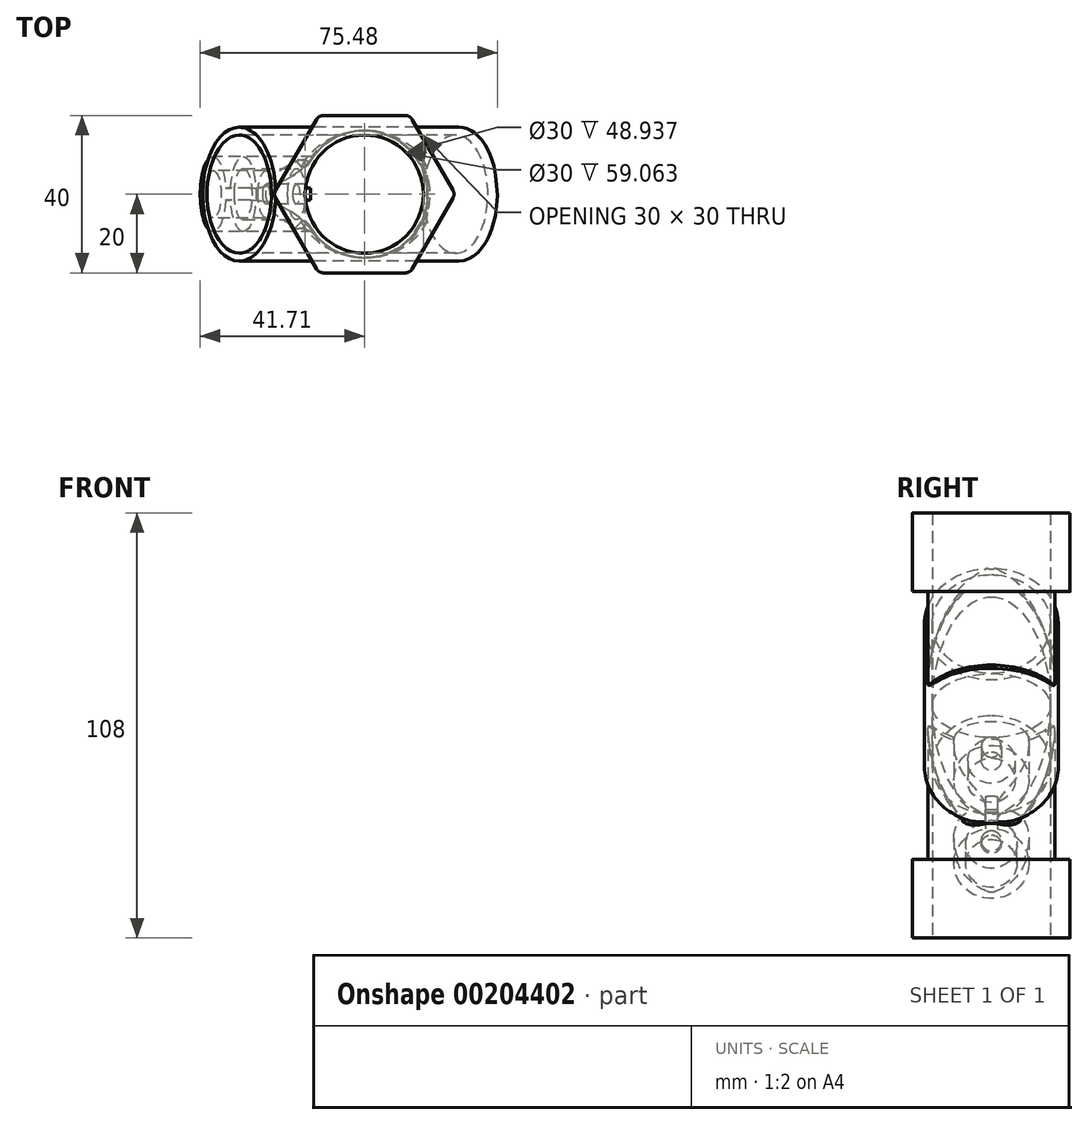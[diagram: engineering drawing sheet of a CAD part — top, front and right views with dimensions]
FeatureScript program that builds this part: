
annotation { "Feature Type Name" : "Feature", "Feature Type Description" : "" }
export const myFeature = defineFeature(function(context is Context, id is Id, definition is map)
    precondition{}
    {
        {
            var Q0;
            Q0=qCreatedBy(makeId("Top.planeOp"),FACE);
            var sketch = newSketch(context, id + "F0", { "sketchPlane" : qUnion([Q0])});
            skCircle(sketch, "E0", {"center": v(0, 0) * mm, "radius": 15 * mm});
            skCircle(sketch, "E1.cCircle", {"center": v(0, 0) * mm, "radius": 20 * mm, "construction": true});
            skLineSegment(sketch, "E1.0", {"start": v(10.4, -20) * mm, "end": v(-10.4, -20) * mm});
            skLineSegment(sketch, "E1.1", {"start": v(-12.12, -19) * mm, "end": v(-22.52, -1) * mm});
            skLineSegment(sketch, "E1.2", {"start": v(-22.52, 1) * mm, "end": v(-12.12, 19) * mm});
            skLineSegment(sketch, "E1.3", {"start": v(-10.4, 20) * mm, "end": v(10.4, 20) * mm});
            skLineSegment(sketch, "E1.4", {"start": v(12.12, 19) * mm, "end": v(22.52, 1) * mm});
            skLineSegment(sketch, "E1.5", {"start": v(22.52, -1) * mm, "end": v(12.12, -19) * mm});
            skPoint(sketch, "E1.0.midPoint", {"position": v(0, -20) * mm});
            skPoint(sketch, "E2.visualSharp", {"position": v(-23.1, 0) * mm});
            skArc(sketch, "E2.filletArc", {"start": v(-22.52, 1) * mm, "mid": v(-22.78, 0) * mm, "end": v(-22.52, -1) * mm});
            skPoint(sketch, "E3.visualSharp", {"position": v(-11.55, -20) * mm});
            skArc(sketch, "E3.filletArc", {"start": v(-12.12, -19) * mm, "mid": v(-11.4, -19.73) * mm, "end": v(-10.4, -20) * mm});
            skPoint(sketch, "E4.visualSharp", {"position": v(11.55, -20) * mm});
            skArc(sketch, "E4.filletArc", {"start": v(10.4, -20) * mm, "mid": v(11.4, -19.73) * mm, "end": v(12.12, -19) * mm});
            skPoint(sketch, "E5.visualSharp", {"position": v(23.1, 0) * mm});
            skArc(sketch, "E5.filletArc", {"start": v(22.52, -1) * mm, "mid": v(22.78, 0) * mm, "end": v(22.52, 1) * mm});
            skPoint(sketch, "E6.visualSharp", {"position": v(11.55, 20) * mm});
            skArc(sketch, "E6.filletArc", {"start": v(12.12, 19) * mm, "mid": v(11.4, 19.73) * mm, "end": v(10.4, 20) * mm});
            skPoint(sketch, "E7.visualSharp", {"position": v(-11.55, 20) * mm});
            skArc(sketch, "E7.filletArc", {"start": v(-10.4, 20) * mm, "mid": v(-11.4, 19.73) * mm, "end": v(-12.12, 19) * mm});
            skSolve(sketch);
        }
        {
            var Q0;
            Q0=makeQuery(id+"F0.imprint","IMPRINT",FACE,{"disambiguationData":[TD([[makeQuery(id+"F0.imprint","IMPRINT",EDGE,{"derivedFrom":sQuery(id+"F0.wireOp",EDGE,"E0")}),-1.0]])]});
            extrude(context, id + "F1", {"entities" : qUnion([Q0]), "depth" : 20 * mm});
        }
        {
            var Q0;
            Q0=makeQuery(id+"F1.opExtrude","CAP_FACE",FACE,{"disambiguationData":[OSD([sQuery(id+"F0.wireOp",EDGE,"E0"),sQuery(id+"F0.wireOp",EDGE,"E1.0"),sQuery(id+"F0.wireOp",EDGE,"E1.1"),sQuery(id+"F0.wireOp",EDGE,"E1.2"),sQuery(id+"F0.wireOp",EDGE,"E1.3"),sQuery(id+"F0.wireOp",EDGE,"E1.4"),sQuery(id+"F0.wireOp",EDGE,"E1.5"),sQuery(id+"F0.wireOp",EDGE,"E2.filletArc"),sQuery(id+"F0.wireOp",EDGE,"E3.filletArc"),sQuery(id+"F0.wireOp",EDGE,"E4.filletArc"),sQuery(id+"F0.wireOp",EDGE,"E5.filletArc"),sQuery(id+"F0.wireOp",EDGE,"E6.filletArc"),sQuery(id+"F0.wireOp",EDGE,"E7.filletArc")])],"isStart":false});
            var sketch = newSketch(context, id + "F2", { "sketchPlane" : qUnion([Q0])});
            skCircle(sketch, "E8", {"center": v(0, 0) * mm, "radius": 16.15 * mm});
            skCircle(sketch, "E9", {"center": v(0, 0) * mm, "radius": 9 * mm});
            skSolve(sketch);
        }
        {
            var Q0;
            Q0=makeQuery(id+"F2.imprint","IMPRINT",FACE,{"disambiguationData":[TD([[makeQuery(id+"F2.imprint","IMPRINT",EDGE,{"derivedFrom":sQuery(id+"F2.wireOp",EDGE,"E8")}),1.0]])]});
            var Q1;
            Q1=makeQuery(id+"F2.imprint","IMPRINT",FACE,{"disambiguationData":[TD([[makeQuery(id+"F2.imprint","IMPRINT",EDGE,{"derivedFrom":sQuery(id+"F2.wireOp",EDGE,"E9")}),-1.0]])]});
            extrude(context, id + "F3", {"entities" : qUnion([Q0, Q1]), "operationType" : NewBodyOperationType.ADD, "depth" : 34 * mm});
        }
        {
            var Q0;
            Q0=makeQuery(id+"F1.opExtrude","SWEPT_BODY",BODY,{"disambiguationData":[OSD([sQuery(id+"F0.wireOp",EDGE,"E0"),sQuery(id+"F0.wireOp",EDGE,"E1.0"),sQuery(id+"F0.wireOp",EDGE,"E1.1"),sQuery(id+"F0.wireOp",EDGE,"E1.2"),sQuery(id+"F0.wireOp",EDGE,"E1.3"),sQuery(id+"F0.wireOp",EDGE,"E1.4"),sQuery(id+"F0.wireOp",EDGE,"E1.5"),sQuery(id+"F0.wireOp",EDGE,"E2.filletArc"),sQuery(id+"F0.wireOp",EDGE,"E3.filletArc"),sQuery(id+"F0.wireOp",EDGE,"E4.filletArc"),sQuery(id+"F0.wireOp",EDGE,"E5.filletArc"),sQuery(id+"F0.wireOp",EDGE,"E6.filletArc"),sQuery(id+"F0.wireOp",EDGE,"E7.filletArc")])]});
            var Q1;
            Q1=makeQuery(id+"F3.opExtrude","CAP_FACE",FACE,{"disambiguationData":[OSD([sQuery(id+"F2.wireOp",EDGE,"E8"),sQuery(id+"F2.wireOp",EDGE,"E9")])],"isStart":false});
            mirror(context, id + "F4", {"operationType" : NewBodyOperationType.ADD, "entities" : qUnion([Q0]), "mirrorPlane" : qUnion([Q1])});
        }
        {
            var Q0;
            Q0=qCreatedBy(makeId("Front.planeOp"),FACE);
            var sketch = newSketch(context, id + "F5", { "sketchPlane" : qUnion([Q0])});
            skLineSegment(sketch, "E10", {"start": v(-22.52, 94) * mm, "end": v(33.32, 57.66) * mm});
            skLineSegment(sketch, "E11", {"start": v(16.15, 88) * mm, "end": v(16.15, 34) * mm, "construction": true});
            skLineSegment(sketch, "E12", {"start": v(-29.56, 78.3) * mm, "end": v(24.88, 42.87) * mm, "construction": true});
            skLineSegment(sketch, "E13", {"start": v(33.6, 56.28) * mm, "end": v(24.88, 42.87) * mm});
            skLineSegment(sketch, "E14", {"start": v(24.88, 42.87) * mm, "end": v(16.15, 29.46) * mm, "construction": true});
            skLineSegment(sketch, "E15", {"start": v(16.15, 29.46) * mm, "end": v(-42.19, 67.43) * mm, "construction": true});
            skLineSegment(sketch, "E16.0", {"start": v(31.39, 56.53) * mm, "end": v(23.2, 43.96) * mm});
            skLineSegment(sketch, "E16.1", {"start": v(-23.6, 92.32) * mm, "end": v(31.39, 56.53) * mm});
            skLineSegment(sketch, "E17", {"start": v(-22.52, 94) * mm, "end": v(-23.6, 92.32) * mm});
            skLineSegment(sketch, "E18", {"start": v(23.2, 43.96) * mm, "end": v(24.88, 42.87) * mm});
            skPoint(sketch, "E19.visualSharp", {"position": v(34.15, 57.12) * mm});
            skLineSegment(sketch, "E20", {"start": v(-23.6, 92.32) * mm, "end": v(-31.79, 79.75) * mm});
            skLineSegment(sketch, "E21", {"start": v(-31.79, 79.75) * mm, "end": v(23.2, 43.96) * mm});
            skArc(sketch, "E22.filletArc", {"start": v(33.6, 56.28) * mm, "mid": v(33.75, 57.03) * mm, "end": v(33.32, 57.66) * mm});
            skSolve(sketch);
        }
        {
            var Q0;
            Q0=makeQuery(id+"F5.imprint","IMPRINT",FACE,{"disambiguationData":[TD([[makeQuery(id+"F5.imprint","IMPRINT",EDGE,{"derivedFrom":sQuery(id+"F5.wireOp",EDGE,"E10")}),-1.0]])]});
            var Q1;
            Q1=sQuery(id+"F5.wireOp",EDGE,"E12");
            revolve(context, id + "F6", {"entities" : qUnion([Q0]), "axis" : qUnion([Q1]), "revolveType" : RevolveType.FULL});
        }
        {
            var Q0;
            Q0=makeQuery(id+"F5.imprint","IMPRINT",FACE,{"disambiguationData":[TD([[makeQuery(id+"F5.imprint","IMPRINT",EDGE,{"derivedFrom":sQuery(id+"F5.wireOp",EDGE,"E16.0")}),-1.0]])]});
            var Q1;
            Q1=sQuery(id+"F5.wireOp",EDGE,"E21");
            revolve(context, id + "F7", {"operationType" : NewBodyOperationType.REMOVE, "entities" : qUnion([Q0]), "axis" : qUnion([Q1]), "revolveType" : RevolveType.FULL, "oppositeDirection" : true});
        }
        {
            var Q0;
            Q0=makeQuery(id+"F4.opPattern","COPY",FACE,{"derivedFrom":makeQuery(id+"F3.opExtrude","CAP_FACE",FACE,{"disambiguationData":[OSD([sQuery(id+"F2.wireOp",EDGE,"E8"),sQuery(id+"F2.wireOp",EDGE,"E9")])],"isStart":true}),"instanceName":"1"});
            var sketch = newSketch(context, id + "F8", { "sketchPlane" : qUnion([Q0])});
            skCircle(sketch, "E23", {"center": v(0, 0) * mm, "radius": 15 * mm});
            skSolve(sketch);
        }
        {
            var Q0;
            Q0 = qSketchRegion(id + "F8", true);
            extrude(context, id + "F9", {"entities" : qUnion([Q0]), "operationType" : NewBodyOperationType.REMOVE, "depth" : 25 * mm});
        }
        {
            var Q0;
            Q0 = qSketchRegion(id + "F8", true);
            var Q1;
            Q1=makeQuery(id+"F4.opPattern","COPY",FACE,{"derivedFrom":makeQuery(id+"F3.opExtrude","CAP_FACE",FACE,{"disambiguationData":[OSD([sQuery(id+"F2.wireOp",EDGE,"E8"),sQuery(id+"F2.wireOp",EDGE,"E9")])],"isStart":true}),"instanceName":"1"});
            extrude(context, id + "F10", {"entities" : qUnion([Q0, Q1]), "operationType" : NewBodyOperationType.REMOVE, "oppositeDirection" : true, "depth" : 7 * mm});
        }
        {
            var Q0;
            Q0=makeQuery(id+"F6.opRevolve","SWEPT_BODY",BODY,{"disambiguationData":[OSD([sQuery(id+"F5.wireOp",EDGE,"E10"),sQuery(id+"F5.wireOp",EDGE,"E13"),sQuery(id+"F5.wireOp",EDGE,"E16.0"),sQuery(id+"F5.wireOp",EDGE,"E16.1"),sQuery(id+"F5.wireOp",EDGE,"E17"),sQuery(id+"F5.wireOp",EDGE,"E18"),sQuery(id+"F5.wireOp",EDGE,"E19.filletArc")])]});
            var Q1;
            Q1=makeQuery(id+"F1.opExtrude","SWEPT_BODY",BODY,{"disambiguationData":[OSD([sQuery(id+"F0.wireOp",EDGE,"E0"),sQuery(id+"F0.wireOp",EDGE,"E1.0"),sQuery(id+"F0.wireOp",EDGE,"E1.1"),sQuery(id+"F0.wireOp",EDGE,"E1.2"),sQuery(id+"F0.wireOp",EDGE,"E1.3"),sQuery(id+"F0.wireOp",EDGE,"E1.4"),sQuery(id+"F0.wireOp",EDGE,"E1.5"),sQuery(id+"F0.wireOp",EDGE,"E2.filletArc"),sQuery(id+"F0.wireOp",EDGE,"E3.filletArc"),sQuery(id+"F0.wireOp",EDGE,"E4.filletArc"),sQuery(id+"F0.wireOp",EDGE,"E5.filletArc"),sQuery(id+"F0.wireOp",EDGE,"E6.filletArc"),sQuery(id+"F0.wireOp",EDGE,"E7.filletArc")])]});
            booleanBodies(context, id + "F11", {"operationType" : BooleanOperationType.UNION, "tools" : qUnion([Q0, Q1])});
        }
        {
            var Q0;
            Q0=makeQuery(id+"F4.opPattern","COPY",EDGE,{"derivedFrom":makeQuery(id+"F3.opExtrude","CAP_EDGE",EDGE,{"disambiguationData":[OSD([sQuery(id+"F2.wireOp",EDGE,"E8")])],"isStart":true}),"instanceName":"1"});
            var Q1;
            Q1=makeQuery(id+"F3.opExtrude","CAP_EDGE",EDGE,{"disambiguationData":[OSD([sQuery(id+"F2.wireOp",EDGE,"E8")])],"isStart":true});
            var Q2;
            Q2=makeQuery(id+"F4.opPattern","COPY",EDGE,{"derivedFrom":makeQuery(id+"F3.opExtrude","CAP_EDGE",EDGE,{"disambiguationData":[OSD([sQuery(id+"F2.wireOp",EDGE,"E9")])],"isStart":true}),"instanceName":"1"});
            var Q3;
            Q3=makeQuery(id+"F3.opExtrude","CAP_EDGE",EDGE,{"disambiguationData":[OSD([sQuery(id+"F2.wireOp",EDGE,"E9")])],"isStart":true});
            chamfer(context, id + "F12", {"entities" : qUnion([Q0, Q1, Q2, Q3]), "width" : 7 * mm, "tangentPropagation" : true});
        }
        {
            var Q0;
            Q0=qCreatedBy(makeId("Top.planeOp"),FACE);
            var sketch = newSketch(context, id + "F13", { "sketchPlane" : qUnion([Q0])});
            skCircle(sketch, "E24", {"center": v(0, 0) * mm, "radius": 9 * mm});
            skSolve(sketch);
        }
        {
            var Q0;
            Q0 = qSketchRegion(id + "F13", true);
            extrude(context, id + "F14", {"entities" : qUnion([Q0]), "operationType" : NewBodyOperationType.REMOVE, "depth" : 100 * mm});
        }
        {
            var Q0;
            Q0=qCreatedBy(makeId("Front.planeOp"),FACE);
            var sketch = newSketch(context, id + "F15", { "sketchPlane" : qUnion([Q0])});
            skLineSegment(sketch, "E25", {"start": v(0, 90.32) * mm, "end": v(0, -35.6) * mm, "construction": true});
            skLineSegment(sketch, "E26", {"start": v(-32.67, 10) * mm, "end": v(0, 10) * mm, "construction": true});
            skLineSegment(sketch, "E27", {"start": v(-27.52, 10) * mm, "end": v(-39.63, 43.27) * mm, "construction": true});
            skLineSegment(sketch, "E28", {"start": v(-27.52, 10) * mm, "end": v(-0.04, 20) * mm});
            skLineSegment(sketch, "E29", {"start": v(-0.04, 20) * mm, "end": v(-1.2, 23.22) * mm});
            skLineSegment(sketch, "E30", {"start": v(-28.54, 12.82) * mm, "end": v(-27.52, 10) * mm});
            skLineSegment(sketch, "E31", {"start": v(-30.77, 18.93) * mm, "end": v(-9.94, 26.5) * mm, "construction": true});
            skLineSegment(sketch, "E32", {"start": v(-35.21, 31.14) * mm, "end": v(-3.62, 42.64) * mm});
            skLineSegment(sketch, "E33", {"start": v(-38.46, 40.07) * mm, "end": v(-7.1, 51.48) * mm, "construction": true});
            skLineSegment(sketch, "E34", {"start": v(-1.2, 23.22) * mm, "end": v(-2.43, 26.58) * mm});
            skLineSegment(sketch, "E35", {"start": v(-2.43, 26.58) * mm, "end": v(-16.4, 21.5) * mm});
            skLineSegment(sketch, "E36", {"start": v(-16.4, 21.5) * mm, "end": v(-15.02, 17.74) * mm});
            skLineSegment(sketch, "E37", {"start": v(-15.02, 17.74) * mm, "end": v(-28.54, 12.82) * mm});
            skLineSegment(sketch, "E38", {"start": v(-35.21, 31.14) * mm, "end": v(-36.4, 34.42) * mm});
            skLineSegment(sketch, "E39", {"start": v(-36.4, 34.42) * mm, "end": v(-22.88, 39.34) * mm});
            skLineSegment(sketch, "E40", {"start": v(-22.88, 39.34) * mm, "end": v(-24.09, 42.64) * mm});
            skLineSegment(sketch, "E41", {"start": v(-24.09, 42.64) * mm, "end": v(-15.16, 45.89) * mm});
            skLineSegment(sketch, "E42", {"start": v(-12.2, 10) * mm, "end": v(-29.6, 57.79) * mm, "construction": true});
            skLineSegment(sketch, "E43", {"start": v(-15.16, 45.89) * mm, "end": v(-4.37, 49.82) * mm});
            skLineSegment(sketch, "E44", {"start": v(-4.37, 49.82) * mm, "end": v(-1.97, 43.24) * mm});
            skLineSegment(sketch, "E45", {"start": v(-1.97, 43.24) * mm, "end": v(-3.62, 42.64) * mm});
            skSolve(sketch);
        }
        {
            var Q0;
            Q0=makeQuery(id+"F15.imprint","IMPRINT",FACE,{"disambiguationData":[TD([[makeQuery(id+"F15.imprint","IMPRINT",EDGE,{"derivedFrom":sQuery(id+"F15.wireOp",EDGE,"E28")}),1.0]])]});
            var Q1;
            Q1=sQuery(id+"F15.wireOp",EDGE,"E31");
            revolve(context, id + "F16", {"entities" : qUnion([Q0]), "axis" : qUnion([Q1]), "revolveType" : RevolveType.FULL});
        }
        {
            var Q0;
            Q0=makeQuery(id+"F15.imprint","IMPRINT",FACE,{"disambiguationData":[TD([[makeQuery(id+"F15.imprint","IMPRINT",EDGE,{"derivedFrom":sQuery(id+"F15.wireOp",EDGE,"E32")}),1.0]])]});
            var Q1;
            Q1=sQuery(id+"F15.wireOp",EDGE,"E33");
            revolve(context, id + "F17", {"entities" : qUnion([Q0]), "axis" : qUnion([Q1]), "revolveType" : RevolveType.FULL});
        }
        {
            var Q0;
            Q0=makeQuery(id+"F16.opRevolve","SWEPT_FACE",FACE,{"disambiguationData":[OSD([sQuery(id+"F15.wireOp",EDGE,"E36")])]});
            var sketch = newSketch(context, id + "F18", { "sketchPlane" : qUnion([Q0])});
            skCircle(sketch, "E46", {"center": v(0, 28.3) * mm, "radius": 6.5 * mm});
            skSolve(sketch);
        }
        {
            var Q0;
            Q0 = qSketchRegion(id + "F18", true);
            extrude(context, id + "F19", {"entities" : qUnion([Q0]), "operationType" : NewBodyOperationType.REMOVE, "depth" : 25 * mm});
        }
        {
            var Q0;
            Q0=makeQuery(id+"F16.opRevolve","SWEPT_FACE",FACE,{"disambiguationData":[OSD([sQuery(id+"F15.wireOp",EDGE,"E36")])]});
            var sketch = newSketch(context, id + "F20", { "sketchPlane" : qUnion([Q0])});
            skCircle(sketch, "E47", {"center": v(0, 28.3) * mm, "radius": 2.5 * mm});
            skSolve(sketch);
        }
        {
            var Q0;
            Q0 = qSketchRegion(id + "F20", true);
            extrude(context, id + "F21", {"entities" : qUnion([Q0]), "operationType" : NewBodyOperationType.REMOVE, "oppositeDirection" : true, "depth" : 25 * mm});
        }
        {
            var Q0;
            Q0=makeQuery(id+"F1.opExtrude","CAP_FACE",FACE,{"disambiguationData":[OSD([sQuery(id+"F0.wireOp",EDGE,"E0"),sQuery(id+"F0.wireOp",EDGE,"E1.0"),sQuery(id+"F0.wireOp",EDGE,"E1.1"),sQuery(id+"F0.wireOp",EDGE,"E1.2"),sQuery(id+"F0.wireOp",EDGE,"E1.3"),sQuery(id+"F0.wireOp",EDGE,"E1.4"),sQuery(id+"F0.wireOp",EDGE,"E1.5"),sQuery(id+"F0.wireOp",EDGE,"E2.filletArc"),sQuery(id+"F0.wireOp",EDGE,"E3.filletArc"),sQuery(id+"F0.wireOp",EDGE,"E4.filletArc"),sQuery(id+"F0.wireOp",EDGE,"E5.filletArc"),sQuery(id+"F0.wireOp",EDGE,"E6.filletArc"),sQuery(id+"F0.wireOp",EDGE,"E7.filletArc")])],"isStart":true});
            var sketch = newSketch(context, id + "F22", { "sketchPlane" : qUnion([Q0])});
            skCircle(sketch, "E48", {"center": v(0, 0) * mm, "radius": 15 * mm});
            skSolve(sketch);
        }
        {
            var Q0;
            Q0 = qSketchRegion(id + "F22", true);
            extrude(context, id + "F23", {"entities" : qUnion([Q0]), "operationType" : NewBodyOperationType.REMOVE, "oppositeDirection" : true, "depth" : 100 * mm});
        }
        {
            var Q0;
            Q0=makeQuery(id+"F5.imprint","IMPRINT",FACE,{"disambiguationData":[TD([[makeQuery(id+"F5.imprint","IMPRINT",EDGE,{"derivedFrom":sQuery(id+"F5.wireOp",EDGE,"E16.0")}),-1.0]])]});
            var Q1;
            Q1=sQuery(id+"F5.wireOp",EDGE,"E21");
            revolve(context, id + "F24", {"operationType" : NewBodyOperationType.REMOVE, "entities" : qUnion([Q0]), "axis" : qUnion([Q1]), "revolveType" : RevolveType.FULL, "oppositeDirection" : true});
        }
        {
            var Q0;
            Q0=makeQuery(id+"F17.opRevolve","SWEPT_FACE",FACE,{"disambiguationData":[OSD([sQuery(id+"F15.wireOp",EDGE,"E40")])]});
            var sketch = newSketch(context, id + "F25", { "sketchPlane" : qUnion([Q0])});
            skCircle(sketch, "E49", {"center": v(0, 50.8) * mm, "radius": 2.5 * mm});
            skSolve(sketch);
        }
        {
            var Q0;
            Q0 = qSketchRegion(id + "F25", true);
            extrude(context, id + "F26", {"entities" : qUnion([Q0]), "operationType" : NewBodyOperationType.REMOVE, "oppositeDirection" : true, "depth" : 25 * mm});
        }
        {
            var Q0;
            Q0=makeQuery(id+"F17.opRevolve","SWEPT_FACE",FACE,{"disambiguationData":[OSD([sQuery(id+"F15.wireOp",EDGE,"E38")])]});
            var sketch = newSketch(context, id + "F27", { "sketchPlane" : qUnion([Q0])});
            skLineSegment(sketch, "E50.bottom", {"start": v(-1.5, 43.03) * mm, "end": v(1.5, 43.03) * mm});
            skLineSegment(sketch, "E50.top", {"start": v(-1.5, 35.26) * mm, "end": v(1.5, 35.26) * mm});
            skLineSegment(sketch, "E50.left", {"start": v(-1.5, 43.03) * mm, "end": v(-1.5, 35.26) * mm});
            skLineSegment(sketch, "E50.right", {"start": v(1.5, 43.03) * mm, "end": v(1.5, 35.26) * mm});
            skLineSegment(sketch, "E51", {"start": v(-1.5, 39.92) * mm, "end": v(0, 39.92) * mm, "construction": true});
            skLineSegment(sketch, "E52", {"start": v(0, 39.92) * mm, "end": v(1.5, 39.92) * mm, "construction": true});
            skSolve(sketch);
        }
        {
            var Q0;
            Q0 = qSketchRegion(id + "F27", true);
            extrude(context, id + "F28", {"entities" : qUnion([Q0]), "operationType" : NewBodyOperationType.ADD, "oppositeDirection" : true, "depth" : 20.7 * mm});
        }
        {
            var Q0;
            {var subQ0=makeQuery(id+"F3.opExtrude","SWEPT_FACE",FACE,{"disambiguationData":[OSD([sQuery(id+"F2.wireOp",EDGE,"E8")])]});Q0=makeQuery(id+"F28.boolean.opBoolean","INTERSECT",EDGE,{"derivedFrom":[makeQuery(id+"F11.opBoolean","SPLIT",FACE,{"disambiguationData":[TD([makeQuery(id+"F6.opRevolve","SWEPT_FACE",FACE,{"disambiguationData":[OSD([sQuery(id+"F5.wireOp",EDGE,"E13")])]})])],"derivedFrom":makeQuery(id+"F4.boolean.opBoolean","MERGE",FACE,{"derivedFrom":[subQ0,makeQuery(id+"F4.opPattern","COPY",FACE,{"derivedFrom":subQ0,"instanceName":"1"})]})}),makeQuery(id+"F28.opExtrude","SWEPT_FACE",FACE,{"disambiguationData":[OSD([sQuery(id+"F27.wireOp",EDGE,"E50.right")])]})]});}
            var Q1;
            {var subQ0=makeQuery(id+"F3.opExtrude","SWEPT_FACE",FACE,{"disambiguationData":[OSD([sQuery(id+"F2.wireOp",EDGE,"E8")])]});Q1=makeQuery(id+"F28.boolean.opBoolean","INTERSECT",EDGE,{"derivedFrom":[makeQuery(id+"F11.opBoolean","SPLIT",FACE,{"disambiguationData":[TD([makeQuery(id+"F6.opRevolve","SWEPT_FACE",FACE,{"disambiguationData":[OSD([sQuery(id+"F5.wireOp",EDGE,"E13")])]})])],"derivedFrom":makeQuery(id+"F4.boolean.opBoolean","MERGE",FACE,{"derivedFrom":[subQ0,makeQuery(id+"F4.opPattern","COPY",FACE,{"derivedFrom":subQ0,"instanceName":"1"})]})}),makeQuery(id+"F28.opExtrude","SWEPT_FACE",FACE,{"disambiguationData":[OSD([sQuery(id+"F27.wireOp",EDGE,"E50.left")])]})]});}
            fillet(context, id + "F29", {"entities" : qUnion([Q0, Q1]), "radius" : 20 * mm, "tangentPropagation" : true, "allowEdgeOverflow" : false});
        }
        {
            var Q0;
            {var subQ0=makeQuery(id+"F3.opExtrude","SWEPT_FACE",FACE,{"disambiguationData":[OSD([sQuery(id+"F2.wireOp",EDGE,"E8")])]});Q0=makeQuery(id+"F11.opBoolean","INTERSECT",EDGE,{"disambiguationData":[OD(0.0)],"derivedFrom":[makeQuery(id+"F4.boolean.opBoolean","MERGE",FACE,{"derivedFrom":[subQ0,makeQuery(id+"F4.opPattern","COPY",FACE,{"derivedFrom":subQ0,"instanceName":"1"})]}),makeQuery(id+"F6.opRevolve","SWEPT_FACE",FACE,{"disambiguationData":[OSD([sQuery(id+"F5.wireOp",EDGE,"E10")])]})]});}
            var Q1;
            {var subQ0=makeQuery(id+"F3.opExtrude","SWEPT_FACE",FACE,{"disambiguationData":[OSD([sQuery(id+"F2.wireOp",EDGE,"E8")])]});Q1=makeQuery(id+"F26.boolean.opBoolean","SPLIT",EDGE,{"disambiguationData":[OD(0.0)],"derivedFrom":makeQuery(id+"F11.opBoolean","INTERSECT",EDGE,{"disambiguationData":[OD(1.0)],"derivedFrom":[makeQuery(id+"F4.boolean.opBoolean","MERGE",FACE,{"derivedFrom":[subQ0,makeQuery(id+"F4.opPattern","COPY",FACE,{"derivedFrom":subQ0,"instanceName":"1"})]}),makeQuery(id+"F6.opRevolve","SWEPT_FACE",FACE,{"disambiguationData":[OSD([sQuery(id+"F5.wireOp",EDGE,"E10")])]})]})});}
            var Q2;
            {var subQ0=makeQuery(id+"F3.opExtrude","SWEPT_FACE",FACE,{"disambiguationData":[OSD([sQuery(id+"F2.wireOp",EDGE,"E8")])]});var subQ1=makeQuery(id+"F11.opBoolean","SPLIT",FACE,{"disambiguationData":[TD([makeQuery(id+"F6.opRevolve","SWEPT_FACE",FACE,{"disambiguationData":[OSD([sQuery(id+"F5.wireOp",EDGE,"E13")])]})])],"derivedFrom":makeQuery(id+"F4.boolean.opBoolean","MERGE",FACE,{"derivedFrom":[subQ0,makeQuery(id+"F4.opPattern","COPY",FACE,{"derivedFrom":subQ0,"instanceName":"1"})]})});Q2=makeQuery(id+"F29.opFillet","BLEND_EDGE",EDGE,{"blendedFrom":[makeQuery(id+"F28.boolean.opBoolean","INTERSECT",EDGE,{"derivedFrom":[subQ1,makeQuery(id+"F28.opExtrude","SWEPT_FACE",FACE,{"disambiguationData":[OSD([sQuery(id+"F27.wireOp",EDGE,"E50.right")])]})]}),subQ1],"blendedInto":[subQ1]});}
            var Q3;
            {var subQ0=makeQuery(id+"F3.opExtrude","SWEPT_FACE",FACE,{"disambiguationData":[OSD([sQuery(id+"F2.wireOp",EDGE,"E8")])]});var subQ1=makeQuery(id+"F11.opBoolean","SPLIT",FACE,{"disambiguationData":[TD([makeQuery(id+"F6.opRevolve","SWEPT_FACE",FACE,{"disambiguationData":[OSD([sQuery(id+"F5.wireOp",EDGE,"E13")])]})])],"derivedFrom":makeQuery(id+"F4.boolean.opBoolean","MERGE",FACE,{"derivedFrom":[subQ0,makeQuery(id+"F4.opPattern","COPY",FACE,{"derivedFrom":subQ0,"instanceName":"1"})]})});Q3=makeQuery(id+"F29.opFillet","BLEND_EDGE",EDGE,{"blendedFrom":[makeQuery(id+"F28.boolean.opBoolean","INTERSECT",EDGE,{"derivedFrom":[subQ1,makeQuery(id+"F28.opExtrude","SWEPT_FACE",FACE,{"disambiguationData":[OSD([sQuery(id+"F27.wireOp",EDGE,"E50.left")])]})]}),subQ1],"blendedInto":[subQ1]});}
            fillet(context, id + "F30", {"entities" : qUnion([Q0, Q1, Q2, Q3]), "radius" : 1 * mm, "tangentPropagation" : true, "allowEdgeOverflow" : false});
        }
    });
